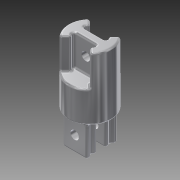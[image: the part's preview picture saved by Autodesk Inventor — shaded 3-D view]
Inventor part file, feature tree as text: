
AUTODESK INVENTOR PART (.ipt)
format: ipt  version: 2013 (Build 170138000, 138)  size: 916,992 bytes
history: native  units: mm
features: extrude x4, other x2, folder x1, plane x1, fillet x1, sketch x1
ambient origin geometry x8: Origin, YZ Plane, XZ Plane, XY Plane, X Axis, Y Axis, Z Axis, Center Point
bodies: Solid1 (feature_tree)
feature tree (10):
  folder  "Master Lengths"
  other  "Profile"
  extrude  "Plug Side"  Depth=2.0mm
  extrude  "Fuse Section"  Depth=12.7mm
  plane  "Work Plane2"
  extrude  "Clamp Side Extrude"  Depth=4.0mm
  fillet  "Fillet1"  [1 undecoded]
  extrude  "Extrusion6"  TaperAngle=45.0deg  [1 undecoded]
  other  "Clamp Side"
  sketch  "Sketch6"  dims[d0=4.0mm d2=2.0mm d3=12.7mm d4=4.0mm d5=45.0deg d6=45.0deg d7=15.0mm d8=0.0mm d9=15.0mm d10=0.0mm d11=0.0mm d12=12.0mm d13=12.0mm d14=15.0mm d16=15.0mm d18=30.0mm d19=25.0mm d21=15.0mm d23=-15.0mm d24=15.0mm d25=0.0mm d26=1.0mm d27=1.0mm d54=4.0mm d56=4.0mm d57=7.5mm d58=7.5mm d59=7.5mm d60=7.5mm d61=0.0mm d62=0.0mm d63=20.0mm d64=0.0mm]
note: 2 required parameter values undecoded (feature->parameter linkage not recoverable at this tier; creation-order binding heuristic only, values carry confidence <= 0.55)
